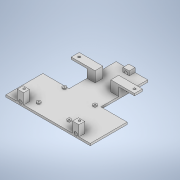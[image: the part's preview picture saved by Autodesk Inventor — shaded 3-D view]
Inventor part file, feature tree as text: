
AUTODESK INVENTOR PART (.ipt)
format: ipt  version: 2020 (Build 240168000, 168)  size: 269,312 bytes
history: native  units: mm
features: sketch x10, extrude x6, hole x5, mirror x1
ambient origin geometry x8: Origin, YZ Plane, XZ Plane, XY Plane, X Axis, Y Axis, Z Axis, Center Point
bodies: Solid1 (feature_tree)
feature tree (22):
  extrude  "Extrusion1"  Depth=30.0mm
  sketch  "Sketch2"  dims[d2=50.0mm d3=70.0mm]
  extrude  "Extrusion2"  Depth=70.0mm
  extrude  "Extrusion4"  Depth=12.0mm
  extrude  "Extrusion5"  Depth=6.0mm
  extrude  "Extrusion6"  Depth=6.0mm
  hole  "Hole5"  [1 undecoded]
  mirror  "Mirror1"
  extrude  "Extrusion3"  Depth=8.0mm
  hole  "Hole3"  [1 undecoded]
  hole  "Hole2"  [1 undecoded]
  hole  "Hole1"  [1 undecoded]
  hole  "Hole4"  [1 undecoded]
  sketch  "Sketch1"  dims[d0=159.0mm d1=30.0mm]
  sketch  "Sketch3"  dims[d4=4.0mm d5=0.0mm d6=12.0mm]
  sketch  "Sketch4"  dims[d7=11.0mm d8=6.0mm]
  sketch  "Sketch5"  dims[d9=8.0mm d10=0.0mm d11=6.0mm]
  sketch  "Sketch6"  dims[d12=6.0mm]
  sketch  "Sketch7"  dims[d13=5.9mm d14=6.0mm d15=6.5mm d16=2.0mm d17=45.0deg d18=8.0mm d19=0.0mm d21=6.0mm]
  sketch  "Sketch9"  dims[d22=6.0mm]
  sketch  "Sketch10"  dims[d24=5.9mm d25=6.0mm d26=6.8mm d27=2.0mm d28=45.0deg d29=8.0mm d30=0.0mm d31=58.0mm]
  sketch  "Sketch11"  dims[d32=49.0mm d33=7.0mm d34=2.0mm d35=0.0mm d36=1.8mm d37=6.0mm d38=4.0mm d39=2.0mm d40=90.0deg d41=8.0mm d42=0.0mm d45=42.0mm d50=20.0mm d51=0.0mm d52=46.5mm d53=6.0mm d54=6.0mm d55=4.1mm d56=6.0mm d57=4.0mm d58=2.0mm d59=90.0deg d60=6.0mm d61=0.0mm d63=111.5mm d64=15.0mm d65=15.0mm d66=20.0mm d67=0.0mm d68=4.0mm d69=30.0mm d70=0.0mm d71=7.5mm d72=4.6mm d73=6.0mm d74=4.0mm d75=2.0mm d76=90.0deg d77=6.0mm d78=0.0mm d79=13.0mm d80=7.0mm d81=7.0mm d82=7.5mm]
note: 5 required parameter values undecoded (feature->parameter linkage not recoverable at this tier; creation-order binding heuristic only, values carry confidence <= 0.55)
